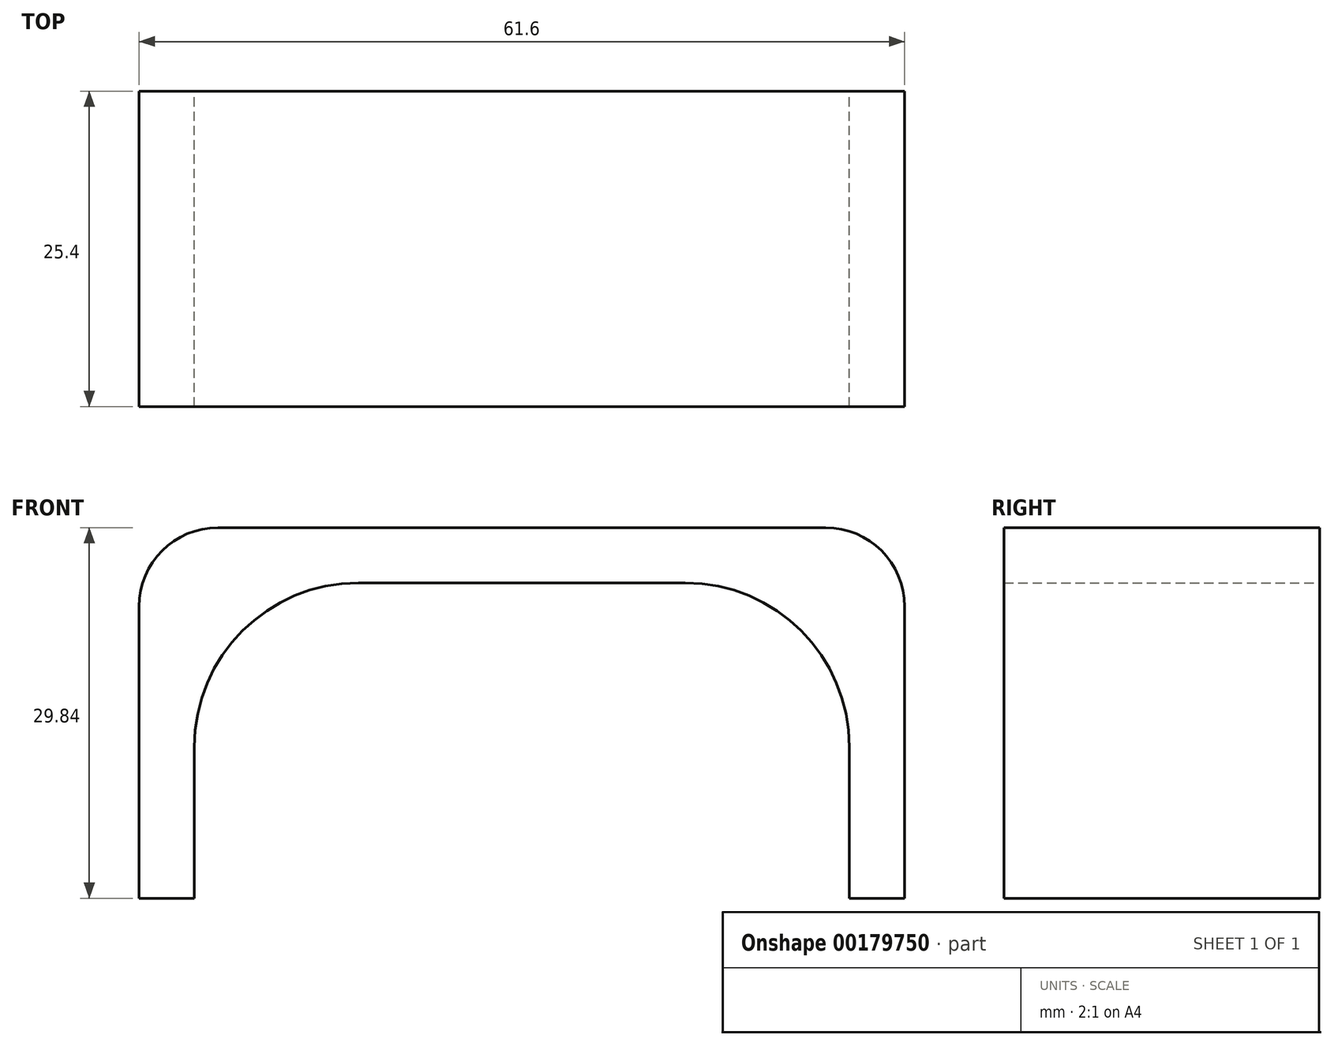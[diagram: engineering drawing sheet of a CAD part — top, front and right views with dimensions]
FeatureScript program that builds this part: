
annotation { "Feature Type Name" : "Feature", "Feature Type Description" : "" }
export const myFeature = defineFeature(function(context is Context, id is Id, definition is map)
    precondition{}
    {
        {
            var Q0;
            Q0=qCreatedBy(makeId("Front.planeOp"),FACE);
            var sketch = newSketch(context, id + "F0", { "sketchPlane" : qUnion([Q0])});
            skLineSegment(sketch, "E0.bottom", {"start": v(0, 0) * mm, "end": v(4.45, 0) * mm});
            skLineSegment(sketch, "E0.top", {"start": v(0, 29.84) * mm, "end": v(61.6, 29.84) * mm});
            skLineSegment(sketch, "E0.left", {"start": v(0, 0) * mm, "end": v(0, 29.84) * mm});
            skLineSegment(sketch, "E0.right", {"start": v(61.6, 0) * mm, "end": v(61.6, 29.85) * mm});
            skLineSegment(sketch, "E1.top", {"start": v(4.44, 25.4) * mm, "end": v(57.15, 25.4) * mm});
            skLineSegment(sketch, "E1.left", {"start": v(4.45, 0) * mm, "end": v(4.44, 25.4) * mm});
            skLineSegment(sketch, "E1.right", {"start": v(57.15, 0) * mm, "end": v(57.15, 25.4) * mm});
            skPoint(sketch, "E2", {"position": v(30.8, 0) * mm});
            skLineSegment(sketch, "E3.trimOffspring", {"start": v(57.15, 0) * mm, "end": v(61.6, 0) * mm});
            skSolve(sketch);
        }
        {
            var Q0;
            Q0=makeQuery(id+"F0.imprint","IMPRINT",FACE,{"disambiguationData":[TD([[makeQuery(id+"F0.imprint","IMPRINT",EDGE,{"derivedFrom":sQuery(id+"F0.wireOp",EDGE,"E0.bottom")}),1.0]])]});
            extrude(context, id + "F1", {"entities" : qUnion([Q0]), "depth" : 25.4 * mm});
        }
        {
            var Q0;
            Q0=makeQuery(id+"F1.opExtrude","SWEPT_EDGE",EDGE,{"disambiguationData":[OSD([sQuery(id+"F0.wireOp",EDGE,"E1.top"),sQuery(id+"F0.wireOp",EDGE,"E1.left")])]});
            var Q1;
            Q1=makeQuery(id+"F1.opExtrude","SWEPT_EDGE",EDGE,{"disambiguationData":[OSD([sQuery(id+"F0.wireOp",EDGE,"E1.top"),sQuery(id+"F0.wireOp",EDGE,"E1.right")])]});
            fillet(context, id + "F2", {"entities" : qUnion([Q0, Q1]), "radius" : 13.2 * mm, "tangentPropagation" : true, "allowEdgeOverflow" : false});
        }
        {
            var Q0;
            Q0=makeQuery(id+"F1.opExtrude","SWEPT_EDGE",EDGE,{"disambiguationData":[OSD([sQuery(id+"F0.wireOp",EDGE,"E0.top"),sQuery(id+"F0.wireOp",EDGE,"E0.left")])]});
            var Q1;
            Q1=makeQuery(id+"F1.opExtrude","SWEPT_EDGE",EDGE,{"disambiguationData":[OSD([sQuery(id+"F0.wireOp",EDGE,"E0.top"),sQuery(id+"F0.wireOp",EDGE,"E0.right")])]});
            fillet(context, id + "F3", {"entities" : qUnion([Q0, Q1]), "radius" : 6.35 * mm, "tangentPropagation" : true, "allowEdgeOverflow" : false});
        }
    });
